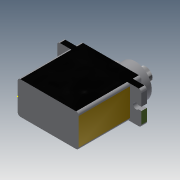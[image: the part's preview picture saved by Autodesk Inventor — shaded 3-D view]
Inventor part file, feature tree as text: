
AUTODESK INVENTOR PART (.ipt)
format: ipt  version: 2013 (Build 170138000, 138)  size: 224,256 bytes
history: native  units: mm
features: sketch x17, fillet x12, extrude x11
ambient origin geometry x8: Origin, YZ Plane, XZ Plane, XY Plane, X Axis, Y Axis, Z Axis, Center Point
bodies: Solid1 (feature_tree)
feature tree (40):
  extrude  "Extrusion1"  Depth=4.4mm TaperAngle=0.0deg
  sketch  "Sketch2"  dims[d11=4.4mm d12=0.0mm d18=7.9mm d19=0.0mm]
  sketch  "Sketch6"  dims[d20=7.9mm d21=0.0mm d22=7.9mm d23=0.0mm]
  extrude  "Extrusion2"  Depth=7.9mm TaperAngle=0.0deg
  sketch  "Sketch7"  dims[d26=4.0mm d27=0.0mm d28=5.0mm]
  sketch  "Sketch8"  dims[d29=3.0mm d30=0.0mm d31=3.0mm d32=0.0mm]
  sketch  "Sketch9"  dims[d39=3.0mm d40=0.0mm d43=3.0mm d44=0.0mm]
  extrude  "Extrusion3"  Depth=7.9mm TaperAngle=0.0deg
  sketch  "Sketch10"  dims[d45=1.0mm d46=1.0mm]
  sketch  "Sketch11"  dims[d47=1.0mm d48=1.0mm]
  extrude  "Extrusion4"  Depth=5.0mm
  extrude  "Extrusion5"  Depth=3.0mm TaperAngle=0.0deg
  extrude  "Extrusion6"  Depth=3.0mm TaperAngle=0.0deg
  extrude  "Extrusion7"  Depth=1.0mm
  extrude  "Extrusion8"  Depth=1.0mm
  extrude  "Extrusion9"  Depth=1.0mm
  sketch  "Sketch16"
  sketch  "Sketch17"
  sketch  "Sketch18"
  sketch  "Sketch19"
  extrude  "Extrusion10"  Depth=1.0mm
  extrude  "Extrusion11"  Depth=1.0mm
  fillet  "Fillet1"  Radius=1.0mm
  sketch  "Sketch20"
  fillet  "Fillet2"  Radius=1.0mm
  fillet  "Fillet3"  [1 undecoded]
  fillet  "Fillet4"  [1 undecoded]
  fillet  "Fillet5"  [1 undecoded]
  fillet  "Fillet6"  [1 undecoded]
  fillet  "Fillet7"  [1 undecoded]
  fillet  "Fillet8"  [1 undecoded]
  fillet  "Fillet9"  [1 undecoded]
  fillet  "Fillet10"  [1 undecoded]
  fillet  "Fillet11"  [1 undecoded]
  fillet  "Fillet12"  [1 undecoded]
  sketch  "Sketch1"  dims[d2=31.7mm d3=0.0mm d7=4.4mm d8=0.0mm]
  sketch  "Sketch12"  dims[d49=1.0mm d50=1.0mm]
  sketch  "Sketch13"  dims[d51=1.0mm d52=1.0mm]
  sketch  "Sketch14"  dims[d53=1.0mm d54=1.0mm d55=1.0mm d56=1.0mm]
  sketch  "Sketch15"
note: 10 required parameter values undecoded (feature->parameter linkage not recoverable at this tier; creation-order binding heuristic only, values carry confidence <= 0.55)
